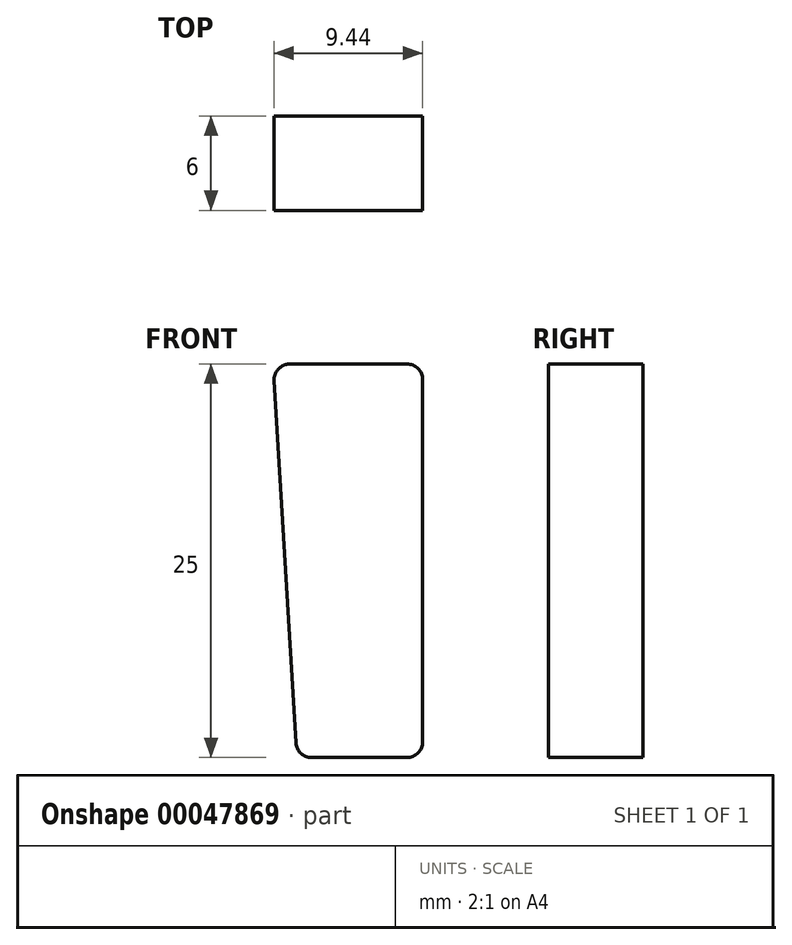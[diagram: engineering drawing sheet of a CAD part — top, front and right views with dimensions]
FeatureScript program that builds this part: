
annotation { "Feature Type Name" : "Feature", "Feature Type Description" : "" }
export const myFeature = defineFeature(function(context is Context, id is Id, definition is map)
    precondition{}
    {
        {
            var Q0;
            Q0=qCreatedBy(makeId("Front.planeOp"),FACE);
            var sketch = newSketch(context, id + "F0", { "sketchPlane" : qUnion([Q0])});
            skLineSegment(sketch, "E0.bottom", {"start": v(-4.93, 10.45) * mm, "end": v(2.51, 10.45) * mm});
            skLineSegment(sketch, "E0.top", {"start": v(-3.55, -14.55) * mm, "end": v(2.51, -14.55) * mm});
            skLineSegment(sketch, "E0.left", {"start": v(-5.92, 9.39) * mm, "end": v(-4.54, -13.61) * mm});
            skLineSegment(sketch, "E0.right", {"start": v(3.51, 9.45) * mm, "end": v(3.51, -13.55) * mm});
            skPoint(sketch, "E1.visualSharp", {"position": v(-5.99, 10.45) * mm});
            skArc(sketch, "E1.filletArc", {"start": v(-4.93, 10.45) * mm, "mid": v(-5.65, 10.13) * mm, "end": v(-5.92, 9.39) * mm});
            skPoint(sketch, "E2.visualSharp", {"position": v(3.51, 10.45) * mm});
            skArc(sketch, "E2.filletArc", {"start": v(3.51, 9.45) * mm, "mid": v(3.22, 10.16) * mm, "end": v(2.51, 10.45) * mm});
            skPoint(sketch, "E3.visualSharp", {"position": v(3.51, -14.55) * mm});
            skArc(sketch, "E3.filletArc", {"start": v(2.51, -14.55) * mm, "mid": v(3.22, -14.26) * mm, "end": v(3.51, -13.55) * mm});
            skPoint(sketch, "E4.visualSharp", {"position": v(-4.49, -14.55) * mm});
            skArc(sketch, "E4.filletArc", {"start": v(-4.54, -13.61) * mm, "mid": v(-4.23, -14.28) * mm, "end": v(-3.55, -14.55) * mm});
            skSolve(sketch);
        }
        {
            var Q0;
            Q0 = qSketchRegion(id + "F0", true);
            extrude(context, id + "F1", {"entities" : qUnion([Q0]), "depth" : 6 * mm});
        }
    });
